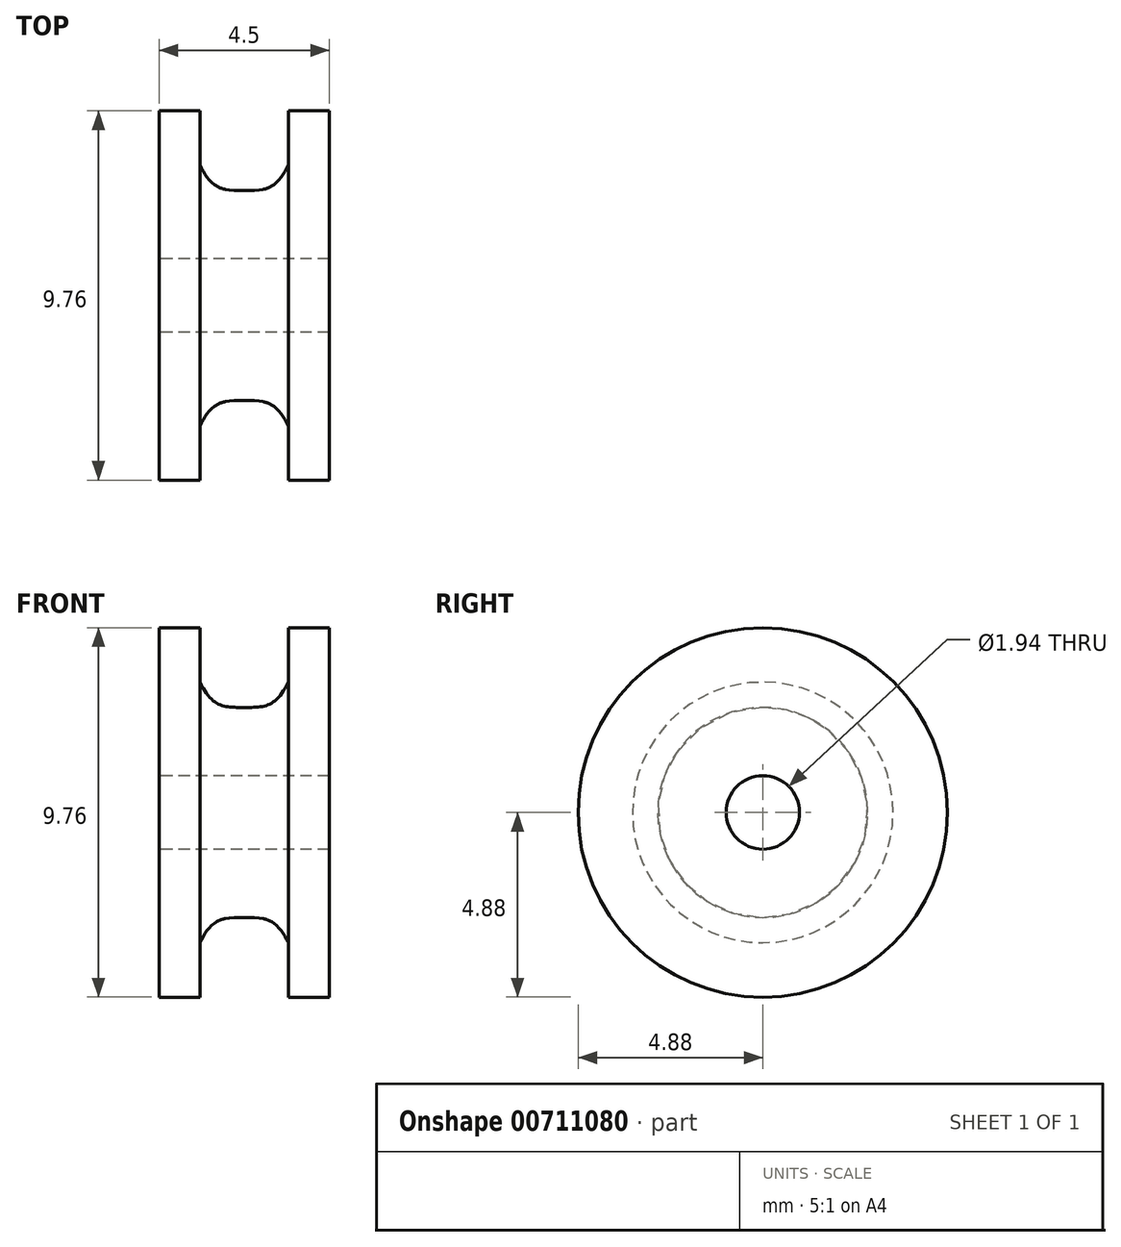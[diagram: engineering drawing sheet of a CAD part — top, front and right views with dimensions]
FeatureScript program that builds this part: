
annotation { "Feature Type Name" : "Feature", "Feature Type Description" : "" }
export const myFeature = defineFeature(function(context is Context, id is Id, definition is map)
    precondition{}
    {
        {
            var Q0;
            Q0=qCreatedBy(makeId("Front.planeOp"),FACE);
            var sketch = newSketch(context, id + "F0", { "sketchPlane" : qUnion([Q0])});
            skLineSegment(sketch, "E0.bottom", {"start": v(-2.25, 4.88) * mm, "end": v(-1.17, 4.88) * mm});
            skLineSegment(sketch, "E0.top", {"start": v(-2.25, -4.88) * mm, "end": v(-1.17, -4.88) * mm});
            skLineSegment(sketch, "E0.left", {"start": v(-2.25, 4.88) * mm, "end": v(-2.25, -4.88) * mm});
            skLineSegment(sketch, "E0.right", {"start": v(-1.17, 4.88) * mm, "end": v(-1.17, -4.88) * mm});
            skPoint(sketch, "E0.middle", {"position": v(-1.7, 0) * mm});
            skFitSpline(sketch, "E1", {"points": [v(-1.17, 3.44) * mm, v(0, 2.78) * mm], "startDerivative": vector(1.02, -2.05) * mm, "endDerivative": vector(1.58, 0) * mm});
            skFitSpline(sketch, "E2.MirrorCS", {"points": [v(-1.17, -3.44) * mm, v(0, -2.78) * mm], "startDerivative": vector(1.02, 2.05) * mm, "endDerivative": vector(1.58, 0) * mm});
            skFitSpline(sketch, "E3.MirrorCS", {"points": [v(1.17, 3.44) * mm, v(0, 2.78) * mm], "startDerivative": vector(-1.02, -2.05) * mm, "endDerivative": vector(-1.58, 0) * mm});
            skLineSegment(sketch, "E4.MirrorCS", {"start": v(1.17, 4.88) * mm, "end": v(1.17, -4.88) * mm});
            skLineSegment(sketch, "E5.MirrorCS", {"start": v(2.25, 4.88) * mm, "end": v(1.17, 4.88) * mm});
            skLineSegment(sketch, "E6.MirrorCS", {"start": v(2.25, 4.88) * mm, "end": v(2.25, -4.88) * mm});
            skFitSpline(sketch, "E7.MirrorCS", {"points": [v(1.17, -3.44) * mm, v(0, -2.78) * mm], "startDerivative": vector(-1.02, 2.05) * mm, "endDerivative": vector(-1.58, 0) * mm});
            skLineSegment(sketch, "E8.MirrorCS", {"start": v(2.25, -4.88) * mm, "end": v(1.17, -4.88) * mm});
            skLineSegment(sketch, "E9", {"start": v(-2.25, 0) * mm, "end": v(2.25, 0) * mm});
            skSolve(sketch);
        }
        {
            var Q0;
            {var subQ1=sQuery(id+"F0.wireOp",EDGE,"E0.bottom");Q0=makeQuery(id+"F0.imprint","IMPRINT",FACE,{"disambiguationData":[TD([[makeQuery(id+"F0.imprint","IMPRINT",EDGE,{"derivedFrom":subQ1}),-1.0]])]});}
            var Q1;
            {var subQ4=sQuery(id+"F0.wireOp",EDGE,"E1");Q1=makeQuery(id+"F0.imprint","IMPRINT",FACE,{"disambiguationData":[TD([[makeQuery(id+"F0.imprint","IMPRINT",EDGE,{"derivedFrom":subQ4}),-1.0]])]});}
            var Q2;
            {var subQ0=sQuery(id+"F0.wireOp",EDGE,"E5.MirrorCS");Q2=makeQuery(id+"F0.imprint","IMPRINT",FACE,{"disambiguationData":[TD([[makeQuery(id+"F0.imprint","IMPRINT",EDGE,{"derivedFrom":subQ0}),1.0]])]});}
            var Q3;
            Q3=sQuery(id+"F0.wireOp",EDGE,"E9");
            revolve(context, id + "F1", {"surfaceOperationType" : NewSurfaceOperationType.NEW, "entities" : qUnion([Q0, Q1, Q2]), "axis" : qUnion([Q3]), "revolveType" : RevolveType.FULL});
        }
        {
            var Q0;
            Q0=makeQuery(id+"F1.opRevolve","SWEPT_FACE",FACE,{"disambiguationData":[OSD([sQuery(id+"F0.wireOp",EDGE,"E0.left")])]});
            var sketch = newSketch(context, id + "F2", { "sketchPlane" : qUnion([Q0])});
            skCircle(sketch, "E10", {"center": v(0, 0) * mm, "radius": 0.97 * mm});
            skSolve(sketch);
        }
        {
            var Q0;
            Q0=makeQuery(id+"F2.imprint","IMPRINT",FACE,{"disambiguationData":[TD([[makeQuery(id+"F2.imprint","IMPRINT",EDGE,{"derivedFrom":sQuery(id+"F2.wireOp",EDGE,"E10")}),1.0]])]});
            extrude(context, id + "F3", {"entities" : qUnion([Q0]), "operationType" : NewBodyOperationType.REMOVE, "oppositeDirection" : true, "depth" : 25.4 * mm, "offsetDistance" : 25.4 * mm});
        }
    });
